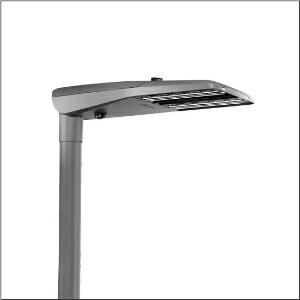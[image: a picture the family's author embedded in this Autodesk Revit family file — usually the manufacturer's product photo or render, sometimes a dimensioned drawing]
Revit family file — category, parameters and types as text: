
# Revit family: streetlight_sl_11_iq_midi___st1_2a_5xc3a61y08me_9d9d
name_source: partatom
category: Lighting Fixtures
units: mm (PartAtom-declared; Revit-internal decimal feet)

## family parameters
Cut with Voids When Loaded = No
Host = Face
Light Source = No
Part Type = Normal
Room Calculation Point = No
Round Connector Dimension = Use Diameter
Shared = No

## types (1)
- --- (1 x LED, 16240 lm, 122.7 W, 2700K)
    Apparent Load = 123 VA
    CIE Flux Codes = 32 70 96 100 100
    Color Rendering = 70
    Color Temperature = 2700K
    Default Elevation = 1800 mm
    Description = Streetlight SL 11 iQ midi, mast luminaire, primary light control with 3 zone facetted reflector, of plastic, silver coated, highly specular, primary optical cover: cover, of PMMA, transparent, light distribution: ST1.2a, light emission: direct distribution, primary light characteristic: asymmetric, installation type: post-top, side-entry, LED, High Power LED, rated luminous flux: 16.240lm, luminous efficacy: 132lm/W, light colour: 727, colour temperature: 2700K, control: presetting dimming logarithmic, Street-Remote, Auto-Match, Temp-Guard, Lumen-Switch, Night-Set, Smart-Wire, Light-Fading, Desk-Remote (wireless, voltage-free reading and setting of iQ features in the workshop via application-optimized NFC function/RFID function), optimised constant luminous flux control (CLO 2.0), with cable H07RN-F 5x 1.5mm², mains connection: 230..240V, AC, 50/60Hz, connection cable pre-assembled, cable length: 12,5m, start of lifetime: 123W, end of service life: 130W, reduction: 56W, luminaire housing, of diecast aluminium, powder-coated, Siteco® metallic grey (DB 702S), please order mast flange separately, inclination adjustable without tools: 0°, 5°, 10°, 15° (post-top) | 0°, -5°, -10°, -15° (side-entry), sealing non-destructively replaceable, multi-level sealing system, length: 780mm, width: 376mm, height: 118mm, mast flange for spigot size: 42mm (side-entry): 5XC10008XM4, 60/48mm (side-entry/post-top): 5XC10108XM2, 76/60mm (side-entry/post-top): 5XC10108XM1, equipment: Power, Smart Interface below and above, protection rating (complete): IP66, insulation class (complete): insulation class II (safety insulation), certification: CE, ENEC, VDE, UKCA, impact resistance: IK09, permissible operating ambient temperature for outdoor applications: -25..+50°C, standard-compliant lighting for roads and squares, Environmental Product Declaration (EPD) tested and certified by an independent institute, packaging unit: 1 piece

Light Distribution: ST1.2a
    Height = 118 mm
    Lamp = 1 x LED
    Lamp Light Flux = 16240 lm
    Lamp Power = 122.7 W
    Lamp count = 1
    Length = 780 mm
    Luminous efficacy = 132 lm/W
    Manufacturer = Siteco
    ModVariant = No
    Model = 5XC3A61Y08ME
    Number of Poles = 1
    OnlyDefault = Yes
    Power Factor = 1
    Product Name = Streetlight SL 11 iQ midi | ST1.2a
    Product group = mast luminaire | pylon top
    ProductGroupID = 6100
    Protection Class = Protection class II
    Protection Degree = IP 66
    RLX_Detail_Level = 1
    RLX_Emergency_Light_Flux = 0 lm
    RLX_Emergency_Type = 0
    RLX_Emergency_Type_DB = No
    RlxData = <blob elided: 69737 chars, md5=6f880b1d>
    Socket = socket
    Standby Power = 0 W
    System Light Flux = 16241 lm
    System Power = 123 W
    Type Comments = factory setting: luminous flux: 100 % | dim-lin: 254 | 553 mA
    Type Image = l_1004429.jpg
    URL = http://relux.com
    VarID = @adj_082415
    Voltage = 0 V
    Weight = 0.00 kg
    Width = 376 mm

## geometry (parser evidence)
native form markers: Blend x4, Sweep x9
no freeform markers — native parametric forms only
